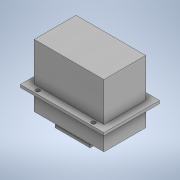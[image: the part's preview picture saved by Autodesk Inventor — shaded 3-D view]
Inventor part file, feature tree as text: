
AUTODESK INVENTOR PART (.ipt)
format: ipt  version: 2022 (Build 260153000, 153)  size: 182,784 bytes
history: native  units: in
note: dims shown in document units (in); Inventor stores cm internally (conversion verified against a paired STEP export)
features: extrude x8, sketch x8
ambient origin geometry x8: Origin, YZ Plane, XZ Plane, XY Plane, X Axis, Y Axis, Z Axis, Center Point
bodies: Solid1 (feature_tree)
feature tree (16):
  extrude  "Extrusion1"  Depth=1.1811in
  extrude  "Extrusion2"  Depth=2.3622in
  extrude  "Extrusion3"  Depth=1.1811in TaperAngle=0.0deg
  extrude  "Extrusion4"  Depth=1.1811in
  extrude  "Extrusion5"  Depth=0.1969in TaperAngle=0.0deg
  extrude  "Extrusion6"  Depth=0.1181in TaperAngle=0.0deg
  extrude  "Extrusion7"  Depth=0.9843in
  extrude  "Extrusion8"  Depth=0.1181in
  sketch  "Sketch1"  dims[d0=1.9685in d1=1.1811in]
  sketch  "Sketch2"  dims[d2=1.9685in d3=0.0in d4=2.3622in]
  sketch  "Sketch3"  dims[d5=1.5748in d6=1.1811in d7=0.0in]
  sketch  "Sketch4"  dims[d8=1.9685in d9=1.1811in]
  sketch  "Sketch5"  dims[d10=1.1024in d11=0.0in d12=0.1969in d13=0.0in]
  sketch  "Sketch6"  dims[d14=0.1969in d15=0.1181in d16=0.0in]
  sketch  "Sketch7"  dims[d19=0.9843in d20=0.9843in]
  sketch  "Sketch8"  dims[d21=0.1181in d22=0.1181in d23=0.1181in d24=0.1181in d25=0.0787in d26=0.0in d27=0.1969in d28=0.1181in d29=0.0in d38=0.1181in d39=0.1181in d40=0.1181in d41=0.1181in d42=0.1181in d43=0.0in]
